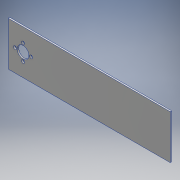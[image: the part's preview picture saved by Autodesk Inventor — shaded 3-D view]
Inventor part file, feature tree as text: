
AUTODESK INVENTOR PART (.ipt)
format: ipt  version: 2016 (Build 200138000, 138)  size: 122,880 bytes
history: native  units: mm
features: extrude x2, sketch x2, other x1
ambient origin geometry x8: Origin, YZ Plane, XZ Plane, XY Plane, X Axis, Y Axis, Z Axis, Center Point
bodies: Body1 (feature_tree)
feature tree (5):
  other  "ソリッド1"
  extrude  "押し出し1"  Depth=220.0mm
  extrude  "押し出し2"  Depth=60.0mm
  sketch  "スケッチ1"
  sketch  "スケッチ2"
